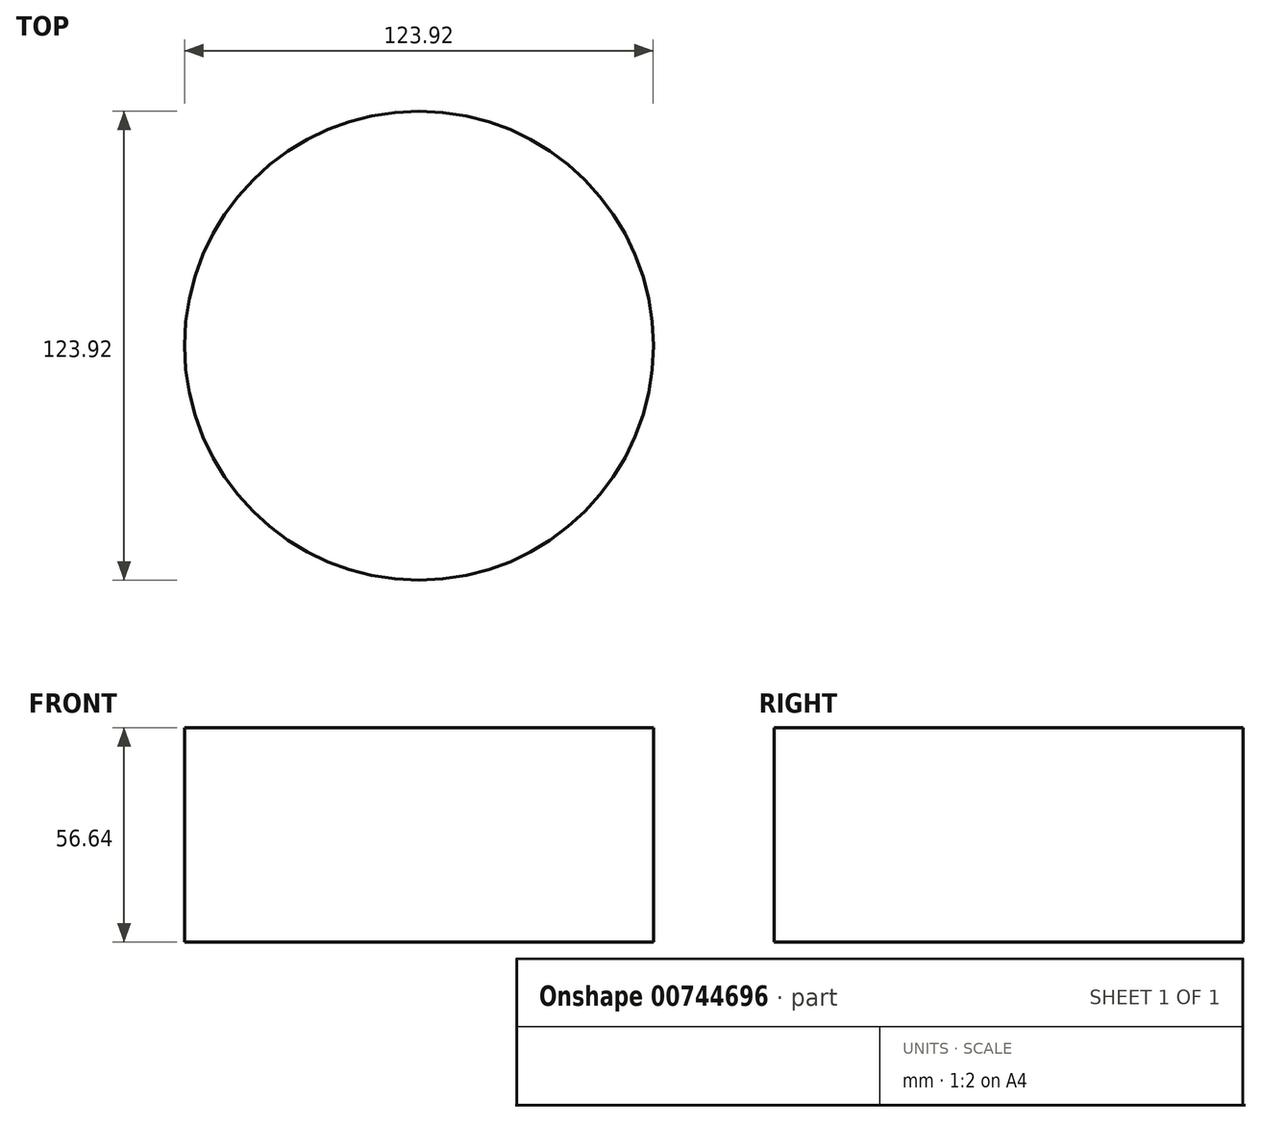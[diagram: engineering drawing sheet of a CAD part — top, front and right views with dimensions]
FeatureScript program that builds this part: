
annotation { "Feature Type Name" : "Feature", "Feature Type Description" : "" }
export const myFeature = defineFeature(function(context is Context, id is Id, definition is map)
    precondition{}
    {
        {
            var Q0;
            Q0=qCreatedBy(makeId("Top.planeOp"),FACE);
            var sketch = newSketch(context, id + "F0", { "sketchPlane" : qUnion([Q0])});
            skCircle(sketch, "E0", {"center": v(0, 0) * mm, "radius": 61.96 * mm});
            skSolve(sketch);
        }
        {
            var Q0;
            Q0=makeQuery(id+"F0.imprint","IMPRINT",FACE,{"disambiguationData":[TD([[makeQuery(id+"F0.imprint","IMPRINT",EDGE,{"derivedFrom":sQuery(id+"F0.wireOp",EDGE,"E0")}),1.0]])]});
            extrude(context, id + "F1", {"entities" : qUnion([Q0]), "depth" : 56.64 * mm, "offsetDistance" : 25.4 * mm});
        }
    });
